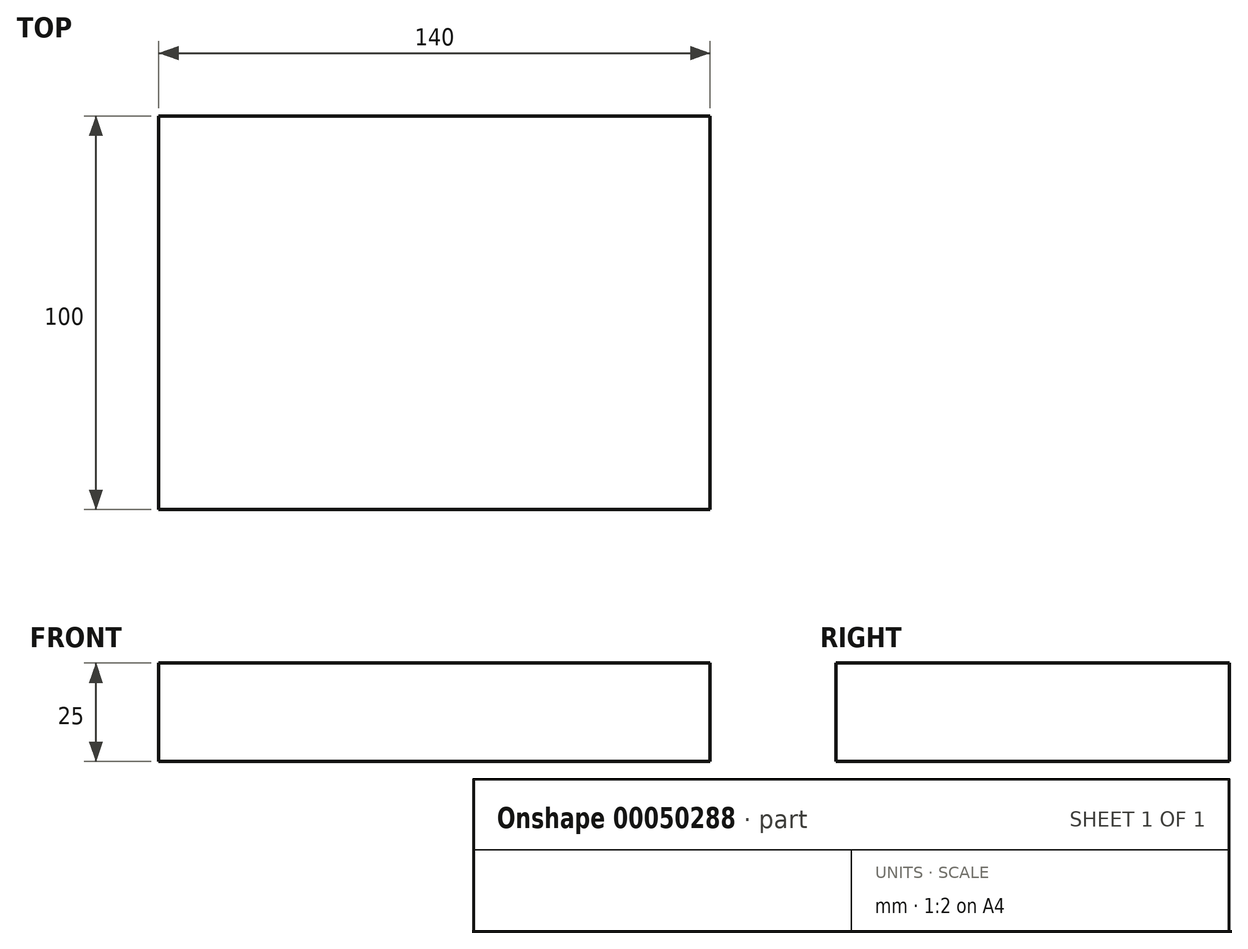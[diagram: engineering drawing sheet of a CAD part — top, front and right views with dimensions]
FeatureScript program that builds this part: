
annotation { "Feature Type Name" : "Feature", "Feature Type Description" : "" }
export const myFeature = defineFeature(function(context is Context, id is Id, definition is map)
    precondition{}
    {
        {
            var Q0;
            Q0=qCreatedBy(makeId("Top.planeOp"),FACE);
            var sketch = newSketch(context, id + "F0", { "sketchPlane" : qUnion([Q0])});
            skLineSegment(sketch, "E0.rect.bottom", {"start": v(70, 50) * mm, "end": v(-70, 50) * mm});
            skLineSegment(sketch, "E0.rect.top", {"start": v(70, -50) * mm, "end": v(-70, -50) * mm});
            skLineSegment(sketch, "E0.rect.left", {"start": v(70, 50) * mm, "end": v(70, -50) * mm});
            skLineSegment(sketch, "E0.rect.right", {"start": v(-70, 50) * mm, "end": v(-70, -50) * mm});
            skPoint(sketch, "E0.rect.middle", {"position": v(0, 0) * mm});
            skSolve(sketch);
        }
        {
            var Q0;
            Q0=makeQuery(id+"F0.imprint","IMPRINT",FACE,{"disambiguationData":[TD([[makeQuery(id+"F0.imprint","IMPRINT",EDGE,{"derivedFrom":sQuery(id+"F0.wireOp",EDGE,"E0.rect.bottom")}),1.0]])]});
            extrude(context, id + "F1", {"entities" : qUnion([Q0]), "depth" : 25 * mm});
        }
    });
